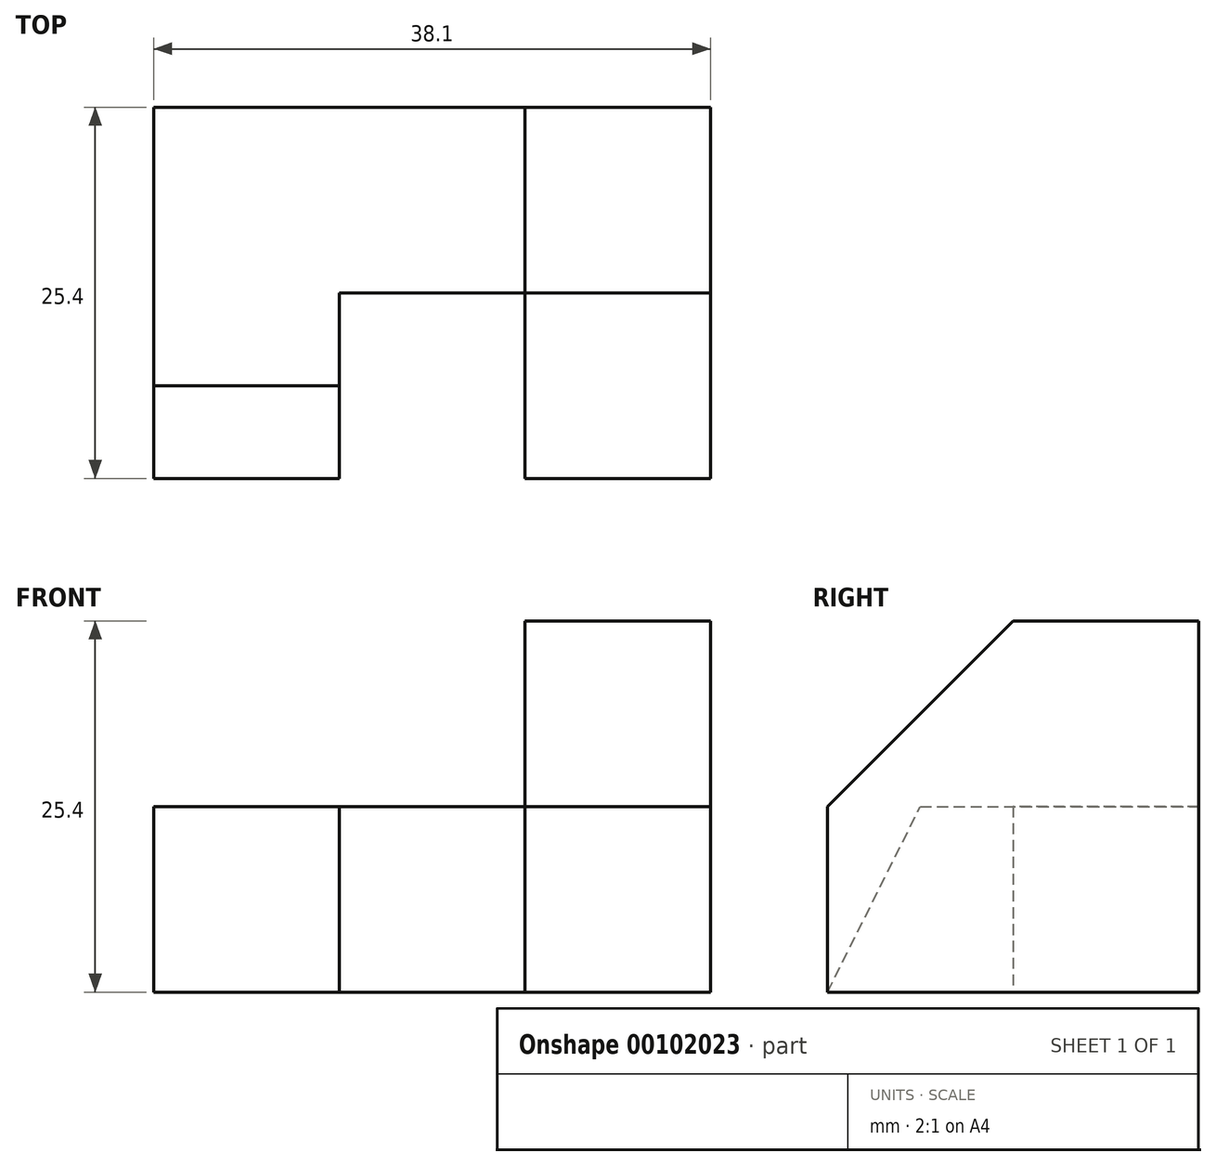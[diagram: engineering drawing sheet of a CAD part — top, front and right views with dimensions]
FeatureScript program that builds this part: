
annotation { "Feature Type Name" : "Feature", "Feature Type Description" : "" }
export const myFeature = defineFeature(function(context is Context, id is Id, definition is map)
    precondition{}
    {
        {
            var Q0;
            Q0=qCreatedBy(makeId("Top.planeOp"),FACE);
            var sketch = newSketch(context, id + "F0", { "sketchPlane" : qUnion([Q0])});
            skLineSegment(sketch, "E0", {"start": v(0, 0) * mm, "end": v(12.7, 0) * mm});
            skLineSegment(sketch, "E1", {"start": v(12.7, 0) * mm, "end": v(12.7, 12.7) * mm});
            skLineSegment(sketch, "E2", {"start": v(12.7, 12.7) * mm, "end": v(25.4, 12.7) * mm});
            skLineSegment(sketch, "E3", {"start": v(25.4, 12.7) * mm, "end": v(25.4, 0) * mm});
            skLineSegment(sketch, "E4", {"start": v(25.4, 0) * mm, "end": v(38.1, 0) * mm});
            skLineSegment(sketch, "E5", {"start": v(38.1, 0) * mm, "end": v(38.1, 25.4) * mm});
            skLineSegment(sketch, "E6", {"start": v(38.1, 25.4) * mm, "end": v(25.4, 25.4) * mm});
            skLineSegment(sketch, "E7", {"start": v(25.4, 25.4) * mm, "end": v(25.4, 12.7) * mm});
            skLineSegment(sketch, "E8", {"start": v(0, 0) * mm, "end": v(0, 25.4) * mm});
            skLineSegment(sketch, "E9", {"start": v(0, 25.4) * mm, "end": v(25.4, 25.4) * mm});
            skSolve(sketch);
        }
        {
            var Q0;
            Q0=makeQuery(id+"F0.imprint","IMPRINT",FACE,{"disambiguationData":[TD([[makeQuery(id+"F0.imprint","IMPRINT",EDGE,{"derivedFrom":sQuery(id+"F0.wireOp",EDGE,"E3")}),1.0]])]});
            extrude(context, id + "F1", {"entities" : qUnion([Q0]), "depth" : 25.4 * mm});
        }
        {
            var Q0;
            Q0 = qSketchRegion(id + "F0", true);
            extrude(context, id + "F2", {"entities" : qUnion([Q0]), "operationType" : NewBodyOperationType.ADD, "depth" : 12.7 * mm});
        }
        {
            var Q0;
            Q0=makeQuery(id+"F2.opExtrude","SWEPT_FACE",FACE,{"disambiguationData":[OSD([sQuery(id+"F0.wireOp",EDGE,"E1")])]});
            var sketch = newSketch(context, id + "F3", { "sketchPlane" : qUnion([Q0])});
            skLineSegment(sketch, "E10", {"start": v(12.7, 12.7) * mm, "end": v(6.35, 12.7) * mm});
            skLineSegment(sketch, "E11", {"start": v(6.35, 12.7) * mm, "end": v(0, 0) * mm});
            skSolve(sketch);
        }
        {
            var Q0;
            {var subQ0=sQuery(id+"F3.wireOp",EDGE,"E11");Q0=makeQuery(id+"F3.imprint","IMPRINT",FACE,{"disambiguationData":[TD([[makeQuery(id+"F3.imprint","IMPRINT",EDGE,{"derivedFrom":subQ0}),-1.0]])]});}
            extrude(context, id + "F4", {"entities" : qUnion([Q0]), "operationType" : NewBodyOperationType.REMOVE, "oppositeDirection" : true, "depth" : 25.4 * mm});
        }
        {
            var Q0;
            Q0=makeQuery(id+"F1.opExtrude","SWEPT_FACE",FACE,{"disambiguationData":[OSD([sQuery(id+"F0.wireOp",EDGE,"E5")])]});
            var sketch = newSketch(context, id + "F5", { "sketchPlane" : qUnion([Q0])});
            skLineSegment(sketch, "E12", {"start": v(12.7, 25.4) * mm, "end": v(0, 12.7) * mm});
            skSolve(sketch);
        }
        {
            var Q0;
            {var subQ0=sQuery(id+"F5.wireOp",EDGE,"E12");Q0=makeQuery(id+"F5.imprint","IMPRINT",FACE,{"disambiguationData":[TD([[makeQuery(id+"F5.imprint","IMPRINT",EDGE,{"derivedFrom":subQ0}),-1.0]])]});}
            extrude(context, id + "F6", {"entities" : qUnion([Q0]), "operationType" : NewBodyOperationType.REMOVE, "oppositeDirection" : true, "depth" : 25.4 * mm});
        }
    });
